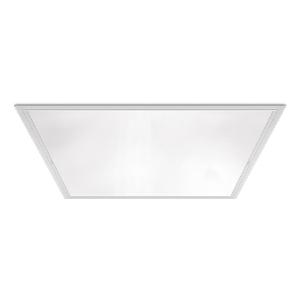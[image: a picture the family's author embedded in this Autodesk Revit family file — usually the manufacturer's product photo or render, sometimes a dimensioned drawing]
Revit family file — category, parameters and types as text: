
# Revit family: 3f_filippi_-_l_600_luce_diffusa_lgs_3f_filippi_-_22839_-_l_600_35w-940_dali_lgs_596x596
name_source: partatom
category: Lighting Fixtures
units: mm (PartAtom-declared; Revit-internal decimal feet)

## family parameters
Cut with Voids When Loaded = No
Host = Face
Light Source = No
Part Type = Normal
Room Calculation Point = No
Round Connector Dimension = Use Diameter
Shared = No

## types (1)
- 3F Filippi - L 600 Luce Diffusa LGS (1 x LED, 3978 lm, 39 W, 4000 K)
    Apparent Load = 39 VA
    Approval mark = ENEC
    CIE Flux Codes = 66 93 98 100 100
    Color Rendering = 90
    Color Temperature = 4000 K
    Control Gear = Electronic transformer
    Default Elevation = 1800 mm
    Description = ILLUMINOTECHNICAL
Luminous efficiency 100% (DLOR 100%, ULOR 0%).
Initial luminous flux of the luminaire 3978 lm.
Direct symmetric distribution.
Installation Interdistance Transv.D = 1.14 x hu - Long.D = 1.16 x hu.
Average luminance <1500 cd/m² for radial angles >65°.
Tabular UGR (CIE 117 - 4H-8H; S=0.25H; 70/50/20): RUG 16.6 - 16.5.
Beam angle: 85° - 85°.
Luminous efficacy 102 lm/W.
Lifetime (L93/B10): 30000 h. (tq+25°C)
Lifetime (L90/B10): 50000 h. (tq+25°C)
Lifetime (L85/B10): 80000 h. (tq+25°C)
Lifetime (L80/B10): 100000 h. (tq+25°C)
Sudden decreased luminous flux after 50000 hours: 0% (C0).
Photobiological safety in compliance with IEC/TR 62778: RG0 risk exempt, (IEC 62471).
In compliance with IEC/EN 62722-2-1 - IEC/EN 62717 standards.

SOURCE
Squared LED module 35W/940.
Source with special protection against aggressive chemically-volatile substances for standard LED technology.
Energy efficiency class (UE 2019/2020 - UE 2019/2015): E.
CIE 13.3 Colour rendering index: CRI >90 (R9 >50%).
IES TM-30 Fidelity Index: Rf = 92 Rg = 101.
CCT nominal colour temperature 4000 K.
Colour initial tolerance (MacAdam): SDCM 3.

MECHANICAL
Housing in galvannealed steel, painted in white epoxy-polyester.
Perimetral frame in white polycarbonate.
LGS micro-prismatic flat diffuser in transparent methacrylate (PMMA), multi-lenticular exterior, anti-glare.
Anti-glare opal polycarbonate filter for brightness uniformity.
Luminaire with limited surface temperature. - D - (EN 60598-2-24)
Dimensions: 596x596 mm, height 95 mm. Weight 5.1 kg.
IP65 protection degree for exposed part, IP64 for recessed part.
Mechanical strength to impacts IK06 (1 joule).
Glow-wire test resistance 650°C.

ELECTRICAL
Halogen Free DALI-2, PUSH-DIM, electronic wiring 230V-50/60Hz, power factor 0.95 at full load, THD <25%, constant output current, class I, 1 driver, 1 DALI addresse.
Power of the luminaire 39 W.
CE - IEC 60598-1 - EN 60598-1.
SAFE FLICKER: PstLM=<1 and SVM=<0.4 (IEC TR 61547-1 and IEC TR 63158), to ensure a more comfortable and safe light.
Luminaire compliant with EN 60598-2-22 for power supply from a centralised emergency system CPSS (Central Power Supply System), not incorporated in the luminaire - high risk areas excluded. The default power and flux are 100% in AC and 15% in DC.
Ambient temperature from 0°C to +40°C.
Temperature class T6 max 85°C.
5-pole terminal block (L-N-PE-DA/DA) quick connection for line connection with connection capacity 2x2.5 mm² per poles.
Relative humidity UR: <85%.

INSTALLATION
Lay-on or pull-up recessed fitting using frame accessory.
All accessories dedicated to this product are available on the Catalog and on our website www.3F-Filippi.com.

APPLICATIONS
Suitable product for food production plants (HACCP), IFS (Food Version 6), BRC (GSFS Food Version 7).
In environments requiring protection and simplified cleaning.
Hospitals, pharmaceutical, chemical, aseptic laboratories, sterilised rooms.
Environments with VDTs.
Environments where demanding visual tasks are performed and soft diffuse light is required for optimal visual comfort and total shielding of the light source.

LIGHT MANAGEMENT
Recommended minimum setting: 10%.
The device, equipped with DALI-2 driver, can be controlled manually with 3F Easy Dim technology or automatically/manually with 3F Smart Dimming technology and/or centralised DALI systems.
DALI-2 certification guarantees interoperability with other devices with the same certification.
In electrical systems without a regulation system (manual or automatic) and DALI bus, a suitable jumper must be made on the DA-DA terminals of the appliance.

WARNING
Luminaire designed for disposal/recycling at end-of-life.
Replaceable (LED only) light source by a professional. Replaceable control gear by a professional.
    Height = 0 mm  [stored 0 ft]
    Lamp = 1 x LED
    Lamp Light Flux = 3978 lm
    Lamp Power = 39 W
    Lamp count = 1
    Length = 596 mm
    Lifetime = 50000 h
    Luminous efficacy = 102 lm/W
    Manufacturer = 3F Filippi
    ModVariant = No
    Model = 3F Filippi - 22839 - L 600 35W-940 DALI LGS 596x596
    Mounting Place = Ceiling
    Mounting Type = Recessed
    Number of Poles = 1
    OnlyDefault = Yes
    Power Factor = 1
    Product Name = 3F Filippi - L 600 Luce Diffusa LGS
    Product group = recessed luminaire
    ProductGroupID = 4
    Protection Class = Protection class I
    Protection Degree = IP 64
    RLX_Detail_Level = 1
    RLX_Emergency_Light_Flux = 0 lm
    RLX_Emergency_Type = 0
    RLX_Emergency_Type_DB = No
    RlxData = <blob elided: 129777 chars, md5=9d5968b0>
    Socket = socket
    Standby Power = 0 W
    System Light Flux = 3978 lm
    System Power = 39 W
    Type Comments = Product without accessories
    Type Image = 3ffilippi_l_600_luce_diffusa_lgs.jpg
    URL = http://relux.com
    VarID = ---
    Voltage = 0 V
    Weight = 0.00 kg
    Width = 596 mm

note: [stored X ft] marks values corroborated as IEEE doubles in the binary element streams (Revit-internal decimal feet)

## geometry (parser evidence)
native form markers: Blend x4, Sweep x9
no freeform markers — native parametric forms only
